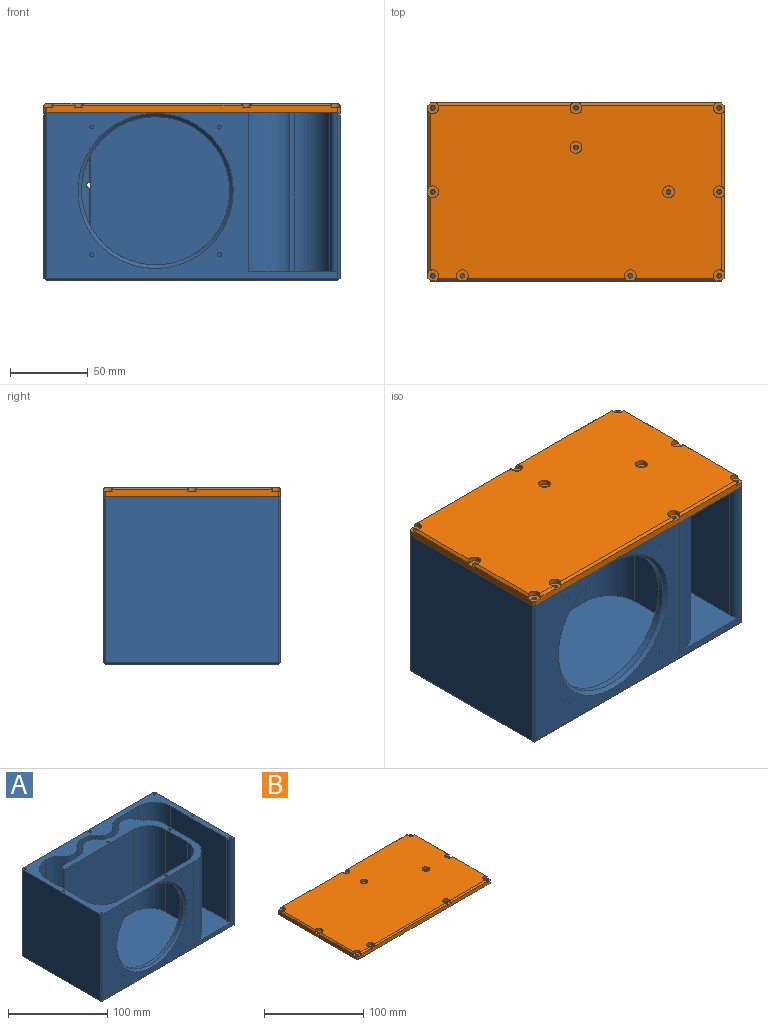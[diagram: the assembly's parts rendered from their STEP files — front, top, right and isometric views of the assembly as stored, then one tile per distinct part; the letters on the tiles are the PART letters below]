
ASSEMBLY  parts=2 mates=1
PART A: 78 faces, bbox 190.5x114.3x108 mm
  f0: plane 44.52x1.43mm, normal (0,-1,0), area 63.5mm2, adj f23,f65,f72,f77
  f1: plane 182.64x107.95mm, normal (0,0,1), area 15454.4mm2, adj f5,f7,f8,f9,f10,f11,f12,f13
  f2: plane 111.3x106.45mm, normal (1,0,0), area 11847.9mm2, adj f23,f45,f46,f49
  f3: plane 187.5x106.45mm, normal (0,1,0), area 19946.8mm2, adj f23,f43,f46,f47,f77
  f4: plane 111.3x106.45mm, normal (-1,0,0), area 11847.9mm2, adj f23,f42,f47,f48
  f5: plane 187.5x106.45mm, normal (0,-1,0), area 6301.2mm2, adj f1,f23,f44,f48,f49,f50,f52,f53
  f6: plane 187.5x111.3mm, normal (0,0,-1), area 20868.8mm2, adj f42,f43,f44,f45
  f7: cylinder r=12.7mm len=101.6mm, axis (0,0,-1), area 2399.2mm2, adj f1,f23,f69,f70
  f8: plane 101.6x29.54mm, normal (0,-1,0), area 3001.7mm2, adj f1,f23,f58,f69
  f9: plane 101.6x78.91mm, normal (-1,0,0), area 8017.4mm2, adj f1,f10,f23,f58
  f10: plane 101.6x0.11mm, normal (-0.97,0.24,0), area 11.3mm2, adj f1,f9,f23,f50
  f11: plane 101.6x41.78mm, normal (1,0,0), area 4245.1mm2, adj f1,f23,f59,f66
  f12: cylinder r=12.7mm len=101.6mm, axis (0,0,-1), area 2718mm2, adj f1,f23,f73,f74
  f13: plane 101.6x0.15mm, normal (0,1,0), area 15.5mm2, adj f1,f23,f74,f75
  f14: cylinder r=12.7mm len=101.6mm, axis (0,0,-1), area 2399.2mm2, adj f1,f23,f75,f76
  f15: plane 101.6x18.19mm, normal (0,1,0), area 1847.8mm2, adj f1,f23,f68,f76
  f16: plane 101.6x99.21mm, normal (0,-1,0), area 10079.8mm2, adj f1,f23,f60,f68
  f17: plane 101.6x30.82mm, normal (-1,0,0), area 3131.6mm2, adj f1,f23,f60,f61
  f18: plane 101.6x99.88mm, normal (0,1,0), area 3138.9mm2, adj f1,f23,f51,f52,f53,f54,f55,f61
  f19: plane 101.6x56.75mm, normal (1,0,0), area 5723.7mm2, adj f1,f23,f62,f63,f64,f65
  f20: plane 53.47x1.43mm, normal (0,-1,0), area 76.3mm2, adj f1,f65,f72,f77
  f21: cylinder r=12.7mm len=101.6mm, axis (0,0,-1), area 2399.2mm2, adj f1,f23,f71,f72
  f22: plane 101.6x0.15mm, normal (0,-1,0), area 15.5mm2, adj f1,f23,f70,f71
  f23: plane 190.5x114.3mm, normal (0,0,1), area 6266.6mm2, adj f0,f2,f3,f4,f5,f7,f8,f9
  f24: cylinder r=1.24mm len=7.62mm, axis (0,0,1), area 59.6mm2, adj f23,f25
  f25: plane 2.49x2.49mm, normal (0,0,1), area 4.9mm2, adj f24
  f26: cylinder r=1.24mm len=7.62mm, axis (0,0,1), area 59.6mm2, adj f23,f27
  f27: plane 2.49x2.49mm, normal (0,0,1), area 4.9mm2, adj f26
  f28: cylinder r=1.24mm len=7.62mm, axis (0,0,1), area 59.6mm2, adj f23,f29
  f29: plane 2.49x2.49mm, normal (0,0,1), area 4.9mm2, adj f28
  f30: cylinder r=1.24mm len=7.62mm, axis (0,0,1), area 59.6mm2, adj f23,f31
  f31: plane 2.49x2.49mm, normal (0,0,1), area 4.9mm2, adj f30
  f32: cylinder r=1.24mm len=7.62mm, axis (0,0,1), area 59.6mm2, adj f23,f33
  f33: plane 2.49x2.49mm, normal (0,0,1), area 4.9mm2, adj f32
  f34: cylinder r=1.24mm len=7.62mm, axis (0,0,1), area 59.6mm2, adj f23,f35
  f35: plane 2.49x2.49mm, normal (0,0,1), area 4.9mm2, adj f34
  f36: cylinder r=1.25mm len=7.62mm, axis (0,0,1), area 59.8mm2, adj f23,f37
  f37: plane 2.5x2.5mm, normal (0,0,1), area 4.9mm2, adj f36
  f38: cylinder r=1.24mm len=7.62mm, axis (0,0,1), area 59.6mm2, adj f23,f39
  f39: plane 2.49x2.49mm, normal (0,0,1), area 4.9mm2, adj f38
  f40: cylinder r=1.24mm len=7.62mm, axis (0,0,1), area 59.6mm2, adj f23,f41
  f41: plane 2.49x2.49mm, normal (0,0,1), area 4.9mm2, adj f40
  f42: plane 112.8x1.5mm, normal (-0.71,0,-0.71), area 237.7mm2, adj f4,f6,f43,f44,f47,f48
  f43: plane 189x1.5mm, normal (0,0.71,-0.71), area 399.3mm2, adj f3,f6,f42,f45,f46,f47
  f44: plane 189x1.5mm, normal (0,-0.71,-0.71), area 399.3mm2, adj f5,f6,f42,f45,f48,f49
  f45: plane 112.8x1.5mm, normal (0.71,0,-0.71), area 237.7mm2, adj f2,f6,f43,f44,f46,f49
  f46: plane 107.2x1.5mm, normal (0.71,0.71,0), area 226.6mm2, adj f2,f3,f23,f43,f45
  f47: plane 107.2x1.5mm, normal (-0.71,0.71,0), area 226.6mm2, adj f3,f4,f23,f42,f43
  f48: plane 107.2x1.5mm, normal (-0.71,-0.71,0), area 226.6mm2, adj f4,f5,f23,f42,f44
  f49: plane 107.2x1.5mm, normal (0.71,-0.71,0), area 226.6mm2, adj f2,f5,f23,f44,f45
  f50: cylinder r=5.02mm len=101.6mm, axis (0,0,1), area 926.4mm2, adj f1,f5,f10,f23
  f51: cylinder r=47.62mm len=95.25mm, axis (0,-1,0), area 1216.1mm2, adj f18,f63,f67
  f52: cylinder r=1.24mm len=6.35mm, axis (0,-1,0), area 49.7mm2, adj f5,f18
  f53: cylinder r=1.24mm len=6.35mm, axis (0,-1,0), area 49.7mm2, adj f5,f18
  f54: cylinder r=1.24mm len=6.35mm, axis (0,-1,0), area 49.7mm2, adj f5,f18
  f55: cylinder r=1.24mm len=6.35mm, axis (0,-1,0), area 49.7mm2, adj f5,f18
  f56: cylinder r=1.24mm len=25.4mm, axis (0,0,1), area 198.6mm2, adj f23,f57
  f57: plane 2.49x2.49mm, normal (0,0,1), area 4.9mm2, adj f56
  f58: cylinder r=22.69mm len=101.6mm, axis (0,0,-1), area 3621mm2, adj f1,f8,f9,f23
  f59: cylinder r=22.69mm len=101.6mm, axis (0,0,-1), area 2119.3mm2, adj f1,f11,f23,f73
  f60: cylinder r=22.69mm len=101.6mm, axis (0,0,-1), area 3621mm2, adj f1,f16,f17,f23
  f61: cylinder r=22.69mm len=101.6mm, axis (0,0,1), area 3621mm2, adj f1,f17,f18,f23
  f62: cylinder r=22.69mm len=30.63mm, axis (0,0,-1), area 1091.5mm2, adj f1,f18,f19,f63
  f63: bspline ~45.38x23.58mm, area 1354.7mm2, adj f19,f51,f62,f64
  f64: cylinder r=22.69mm len=29.13mm, axis (0,0,-1), area 1038mm2, adj f18,f19,f23,f63
  f65: cylinder r=22.69mm len=101.6mm, axis (0,0,1), area 3616.9mm2, adj f0,f1,f19,f20,f23,f77
  f66: cylinder r=26.18mm len=101.6mm, axis (0,0,1), area 4178mm2, adj f1,f5,f11,f23
  f67: cone r=47.62mm half-angle=45deg, axis (0,-1,0), area 990.6mm2, adj f5,f51
  f68: cylinder r=7.36mm len=101.6mm, axis (0,0,-1), area 1071.6mm2, adj f1,f15,f16,f23
  f69: cylinder r=18.9mm len=101.6mm, axis (0,0,-1), area 1785.1mm2, adj f1,f7,f8,f23
  f70: cylinder r=18.9mm len=101.6mm, axis (0,0,-1), area 1785.1mm2, adj f1,f7,f22,f23
  f71: cylinder r=18.9mm len=101.6mm, axis (0,0,-1), area 1785.1mm2, adj f1,f21,f22,f23
  f72: cylinder r=18.9mm len=101.6mm, axis (0,0,-1), area 1782.1mm2, adj f0,f1,f20,f21,f23,f77
  f73: cylinder r=18.9mm len=101.6mm, axis (0,0,1), area 1008.6mm2, adj f1,f12,f23,f59
  f74: cylinder r=18.9mm len=101.6mm, axis (0,0,-1), area 1785.1mm2, adj f1,f12,f13,f23
  f75: cylinder r=18.9mm len=101.6mm, axis (0,0,-1), area 1785.1mm2, adj f1,f13,f14,f23
  f76: cylinder r=18.9mm len=101.6mm, axis (0,0,-1), area 1785.1mm2, adj f1,f14,f15,f23
  f77: cylinder r=2mm len=6.35mm, axis (0,1,0), area 79.8mm2, adj f0,f3,f20,f65,f72
PART B: 54 faces, bbox 190.5x114.3x6.4 mm
  f0: cylinder r=1.5mm len=3.35mm, axis (0,0,-1), area 31.6mm2, adj f25,f33
  f1: cylinder r=1.5mm len=3.35mm, axis (0,0,-1), area 31.6mm2, adj f25,f31
  f2: cylinder r=1.5mm len=3.35mm, axis (0,0,-1), area 31.6mm2, adj f25,f37
  f3: cylinder r=1.5mm len=3.35mm, axis (0,0,-1), area 31.6mm2, adj f25,f35
  f4: cylinder r=1.5mm len=3.35mm, axis (0,0,-1), area 31.5mm2, adj f25,f46
  f5: cylinder r=1.5mm len=3.35mm, axis (0,0,-1), area 31.6mm2, adj f25,f41
  f6: cylinder r=1.5mm len=3.35mm, axis (0,0,-1), area 31.6mm2, adj f25,f43
  f7: cylinder r=1.5mm len=3.35mm, axis (0,0,-1), area 31.6mm2, adj f25,f44
  f8: cylinder r=1.5mm len=3.35mm, axis (0,0,-1), area 31.6mm2, adj f25,f51
  f9: cylinder r=1.5mm len=3.35mm, axis (0,0,-1), area 31.6mm2, adj f25,f49
  f10: cylinder r=1.5mm len=3.35mm, axis (0,0,-1), area 31.5mm2, adj f25,f39
  f11: plane 87.86x1.5mm, normal (0,0.71,0.71), area 183.1mm2, adj f22,f24,f34,f47
  f12: plane 49.76x1.5mm, normal (0.71,0,0.71), area 102.3mm2, adj f21,f24,f36,f45
  f13: plane 49.76x1.5mm, normal (-0.71,0,0.71), area 102.3mm2, adj f23,f24,f32,f42
  f14: plane 103.74x1.5mm, normal (0,-0.71,0.71), area 216.8mm2, adj f20,f24,f38,f40
  f15: plane 14.84x1.5mm, normal (0,-0.71,0.71), area 28.2mm2, adj f20,f24,f30,f38
  f16: plane 3.35x1.5mm, normal (0.71,-0.71,0), area 7.1mm2, adj f20,f21,f25,f37
  f17: plane 3.35x1.5mm, normal (0.71,0.71,0), area 7.1mm2, adj f21,f22,f25,f35
  f18: plane 3.35x1.5mm, normal (-0.71,0.71,0), area 7.1mm2, adj f22,f23,f25,f33
  f19: plane 3.35x1.5mm, normal (-0.71,-0.71,0), area 7.1mm2, adj f20,f23,f25,f31
  f20: plane 187.5x4.85mm, normal (0,-1,0), area 879.4mm2, adj f14,f15,f16,f19,f25,f29,f30,f31
  f21: plane 111.3x4.85mm, normal (1,0,0), area 522.1mm2, adj f12,f16,f17,f25,f27,f34,f35,f36
  f22: plane 187.5x4.85mm, normal (0,1,0), area 891.7mm2, adj f11,f17,f18,f25,f26,f32,f33,f34
  f23: plane 111.3x4.85mm, normal (-1,0,0), area 522.1mm2, adj f13,f18,f19,f25,f28,f30,f31,f32
  f24: plane 187.5x111.3mm, normal (0,0,1), area 20495.7mm2, adj f11,f12,f13,f14,f15,f26,f27,f28
  f25: plane 190.5x114.3mm, normal (0,0,-1), area 21654.1mm2, adj f0,f1,f2,f3,f4,f5,f6,f7
  f26: plane 87.86x1.5mm, normal (0,0.71,0.71), area 183.1mm2, adj f22,f24,f32,f47
  f27: plane 49.76x1.5mm, normal (0.71,0,0.71), area 102.3mm2, adj f21,f24,f34,f45
  f28: plane 49.76x1.5mm, normal (-0.71,0,0.71), area 102.3mm2, adj f23,f24,f30,f42
  f29: plane 52.94x1.5mm, normal (0,-0.71,0.71), area 109mm2, adj f20,f24,f36,f40
  f30: cylinder r=3.81mm len=6.99mm, axis (0,0,1), area 37.2mm2, adj f15,f20,f23,f24,f28,f31
  f31: plane 6.99x6.99mm, normal (0,0,1), area 34.3mm2, adj f1,f19,f20,f23,f30
  f32: cylinder r=3.81mm len=6.99mm, axis (0,0,1), area 37.2mm2, adj f13,f22,f23,f24,f26,f33
  f33: plane 6.99x6.99mm, normal (0,0,1), area 34.3mm2, adj f0,f18,f22,f23,f32
  f34: cylinder r=3.81mm len=6.99mm, axis (0,0,1), area 37.2mm2, adj f11,f21,f22,f24,f27,f35
  f35: plane 6.99x6.99mm, normal (0,0,1), area 34.3mm2, adj f3,f17,f21,f22,f34
  f36: cylinder r=3.81mm len=6.99mm, axis (0,0,1), area 37.2mm2, adj f12,f20,f21,f24,f29,f37
  f37: plane 6.99x6.99mm, normal (0,0,1), area 34.3mm2, adj f2,f16,f20,f21,f36
  f38: cylinder r=3.81mm len=7.62mm, axis (0,0,1), area 55.2mm2, adj f14,f15,f20,f24,f39
  f39: plane 7.62x6.99mm, normal (0,0,1), area 36.7mm2, adj f10,f20,f38
  f40: cylinder r=3.81mm len=7.62mm, axis (0,0,1), area 55.2mm2, adj f14,f20,f24,f29,f41
  f41: plane 7.62x6.99mm, normal (0,0,1), area 36.7mm2, adj f5,f20,f40
  f42: cylinder r=3.81mm len=7.62mm, axis (0,0,1), area 55.2mm2, adj f13,f23,f24,f28,f43
  f43: plane 7.62x6.99mm, normal (0,0,1), area 36.7mm2, adj f6,f23,f42
  f44: plane 7.62x6.99mm, normal (0,0,1), area 36.7mm2, adj f7,f21,f45
  f45: cylinder r=3.81mm len=7.62mm, axis (0,0,1), area 55.2mm2, adj f12,f21,f24,f27,f44
  f46: plane 7.62x6.99mm, normal (0,0,1), area 36.7mm2, adj f4,f22,f47
  f47: cylinder r=3.81mm len=7.62mm, axis (0,0,1), area 55.2mm2, adj f11,f22,f24,f26,f46
  f48: cylinder r=3.81mm len=7.62mm, axis (0,0,1), area 71.8mm2, adj f24,f49
  f49: plane 7.62x7.62mm, normal (0,0,1), area 38.5mm2, adj f9,f48
  f50: cylinder r=3.81mm len=7.62mm, axis (0,0,1), area 71.8mm2, adj f24,f51
  f51: plane 7.62x7.62mm, normal (0,0,1), area 38.5mm2, adj f8,f50
  f52: cylinder r=94.74mm len=18.9mm, axis (0,-1,0), area 37.9mm2, adj f20,f25,f53
  f53: plane 18.9x0.47mm, normal (0,-1,0), area 6mm2, adj f25,f52
PLACE A t=(26.76,-11.23,-8.89)mm
PLACE B t=(26.76,-11.23,99.06)mm
MATE revolute B.f1 <-> A.f38  axis (0,0,-1) through (-65.31,-65.2,99.06)mm
